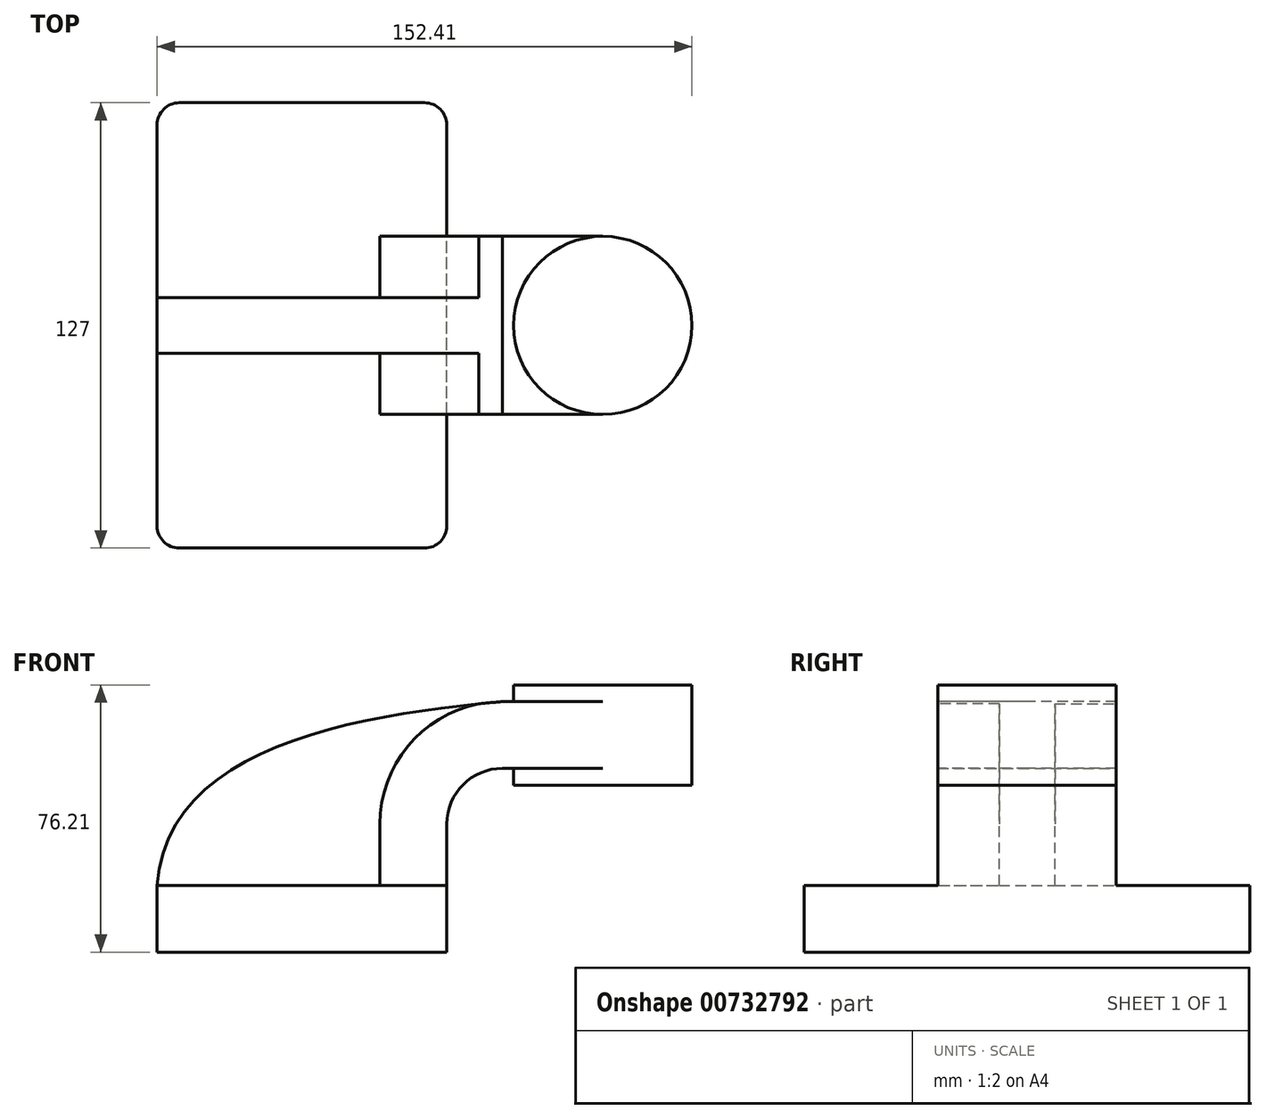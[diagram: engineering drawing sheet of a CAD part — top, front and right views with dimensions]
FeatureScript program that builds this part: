
annotation { "Feature Type Name" : "Feature", "Feature Type Description" : "" }
export const myFeature = defineFeature(function(context is Context, id is Id, definition is map)
    precondition{}
    {
        {
            var Q0;
            Q0=qCreatedBy(makeId("Front.planeOp"),FACE);
            var sketch = newSketch(context, id + "F0", { "sketchPlane" : qUnion([Q0])});
            skLineSegment(sketch, "E0.bottom", {"start": v(-41.27, -9.53) * mm, "end": v(41.28, -9.53) * mm});
            skLineSegment(sketch, "E0.top", {"start": v(-41.28, 9.53) * mm, "end": v(41.28, 9.53) * mm});
            skLineSegment(sketch, "E0.left", {"start": v(-41.28, -9.53) * mm, "end": v(-41.28, 9.53) * mm});
            skLineSegment(sketch, "E0.right", {"start": v(41.28, -9.53) * mm, "end": v(41.28, 9.52) * mm});
            skPoint(sketch, "E0.middle", {"position": v(0, 0) * mm});
            skLineSegment(sketch, "E1.bottom", {"start": v(60.32, 38.1) * mm, "end": v(111.12, 38.1) * mm});
            skLineSegment(sketch, "E1.top", {"start": v(60.32, 66.68) * mm, "end": v(111.12, 66.68) * mm});
            skLineSegment(sketch, "E1.left", {"start": v(60.32, 38.1) * mm, "end": v(60.32, 66.68) * mm});
            skLineSegment(sketch, "E1.right", {"start": v(111.12, 38.1) * mm, "end": v(111.12, 66.68) * mm});
            skPoint(sketch, "E1.middle", {"position": v(85.72, 52.39) * mm});
            skLineSegment(sketch, "E2", {"start": v(41.28, 9.52) * mm, "end": v(41.28, 27) * mm});
            skArc(sketch, "E3", {"start": v(41.27, 27) * mm, "mid": v(45.92, 38.23) * mm, "end": v(57.15, 42.88) * mm});
            skLineSegment(sketch, "E4", {"start": v(57.15, 42.88) * mm, "end": v(85.72, 42.88) * mm});
            skLineSegment(sketch, "E5.0", {"start": v(57.15, 61.93) * mm, "end": v(85.72, 61.93) * mm});
            skArc(sketch, "E5.1", {"start": v(22.22, 27) * mm, "mid": v(32.45, 51.7) * mm, "end": v(57.15, 61.93) * mm});
            skLineSegment(sketch, "E5.2", {"start": v(22.22, 9.52) * mm, "end": v(22.22, 27) * mm});
            skLineSegment(sketch, "E6", {"start": v(85.72, 38.1) * mm, "end": v(85.72, 66.68) * mm});
            skFitSpline(sketch, "E7", {"points": [v(-41.28, 9.53) * mm, v(57.15, 61.93) * mm], "startDerivative": vector(8.82, 119.78) * mm, "endDerivative": vector(124.5, 11.51) * mm});
            skSolve(sketch);
        }
        {
            var Q0;
            Q0=makeQuery(id+"F0.imprint","IMPRINT",FACE,{"disambiguationData":[TD([[makeQuery(id+"F0.imprint","IMPRINT",EDGE,{"derivedFrom":sQuery(id+"F0.wireOp",EDGE,"E0.bottom")}),1.0]])]});
            extrude(context, id + "F1", {"entities" : qUnion([Q0]), "endBound" : BoundingType.SYMMETRIC, "depth" : 127 * mm, "offsetDistance" : 25.4 * mm});
        }
        {
            var Q0;
            {var subQ1=sQuery(id+"F0.wireOp",EDGE,"E2");Q0=makeQuery(id+"F0.imprint","IMPRINT",FACE,{"disambiguationData":[TD([[makeQuery(id+"F0.imprint","IMPRINT",EDGE,{"derivedFrom":subQ1}),1.0]])]});}
            var Q1;
            {var subQ0=sQuery(id+"F0.wireOp",EDGE,"E4");var subQ1=sQuery(id+"F0.wireOp",EDGE,"E1.left");var subQ2=makeQuery(id+"F0.imprint","INTERSECT",VERTEX,{"derivedFrom":[subQ1,subQ0]});Q1=makeQuery(id+"F0.imprint","IMPRINT",FACE,{"disambiguationData":[TD([[makeQuery(id+"F0.imprint","IMPRINT",EDGE,{"disambiguationData":[TD([[subQ2,-1.0]])],"derivedFrom":subQ1}),-1.0]])]});}
            extrude(context, id + "F2", {"entities" : qUnion([Q0, Q1]), "operationType" : NewBodyOperationType.ADD, "endBound" : BoundingType.SYMMETRIC, "depth" : 50.8 * mm, "offsetDistance" : 25.4 * mm});
        }
        {
            var Q0;
            {var subQ3=sQuery(id+"F0.wireOp",EDGE,"E5.2");Q0=makeQuery(id+"F0.imprint","IMPRINT",FACE,{"disambiguationData":[TD([[makeQuery(id+"F0.imprint","IMPRINT",EDGE,{"derivedFrom":subQ3}),1.0]])]});}
            extrude(context, id + "F3", {"entities" : qUnion([Q0]), "operationType" : NewBodyOperationType.ADD, "endBound" : BoundingType.SYMMETRIC, "depth" : 15.88 * mm, "offsetDistance" : 25.4 * mm});
        }
        {
            var Q0;
            {var subQ4=sQuery(id+"F0.wireOp",EDGE,"E1.right");Q0=makeQuery(id+"F0.imprint","IMPRINT",FACE,{"disambiguationData":[TD([[makeQuery(id+"F0.imprint","IMPRINT",EDGE,{"derivedFrom":subQ4}),1.0]])]});}
            var Q1;
            Q1=sQuery(id+"F0.wireOp",EDGE,"E6");
            revolve(context, id + "F4", {"operationType" : NewBodyOperationType.ADD, "surfaceOperationType" : NewSurfaceOperationType.NEW, "entities" : qUnion([Q0]), "axis" : qUnion([Q1]), "revolveType" : RevolveType.FULL});
        }
        {
            var Q0;
            Q0=makeQuery(id+"F1.opExtrude","CAP_EDGE",EDGE,{"disambiguationData":[OSD([sQuery(id+"F0.wireOp",EDGE,"E0.right")])],"isStart":false});
            var Q1;
            Q1=makeQuery(id+"F1.opExtrude","CAP_EDGE",EDGE,{"disambiguationData":[OSD([sQuery(id+"F0.wireOp",EDGE,"E0.left")])],"isStart":false});
            var Q2;
            Q2=makeQuery(id+"F1.opExtrude","CAP_EDGE",EDGE,{"disambiguationData":[OSD([sQuery(id+"F0.wireOp",EDGE,"E0.right")])],"isStart":true});
            var Q3;
            Q3=makeQuery(id+"F1.opExtrude","CAP_EDGE",EDGE,{"disambiguationData":[OSD([sQuery(id+"F0.wireOp",EDGE,"E0.left")])],"isStart":true});
            fillet(context, id + "F5", {"entities" : qUnion([Q0, Q1, Q2, Q3]), "radius" : 6.35 * mm, "tangentPropagation" : true, "allowEdgeOverflow" : false});
        }
    });
